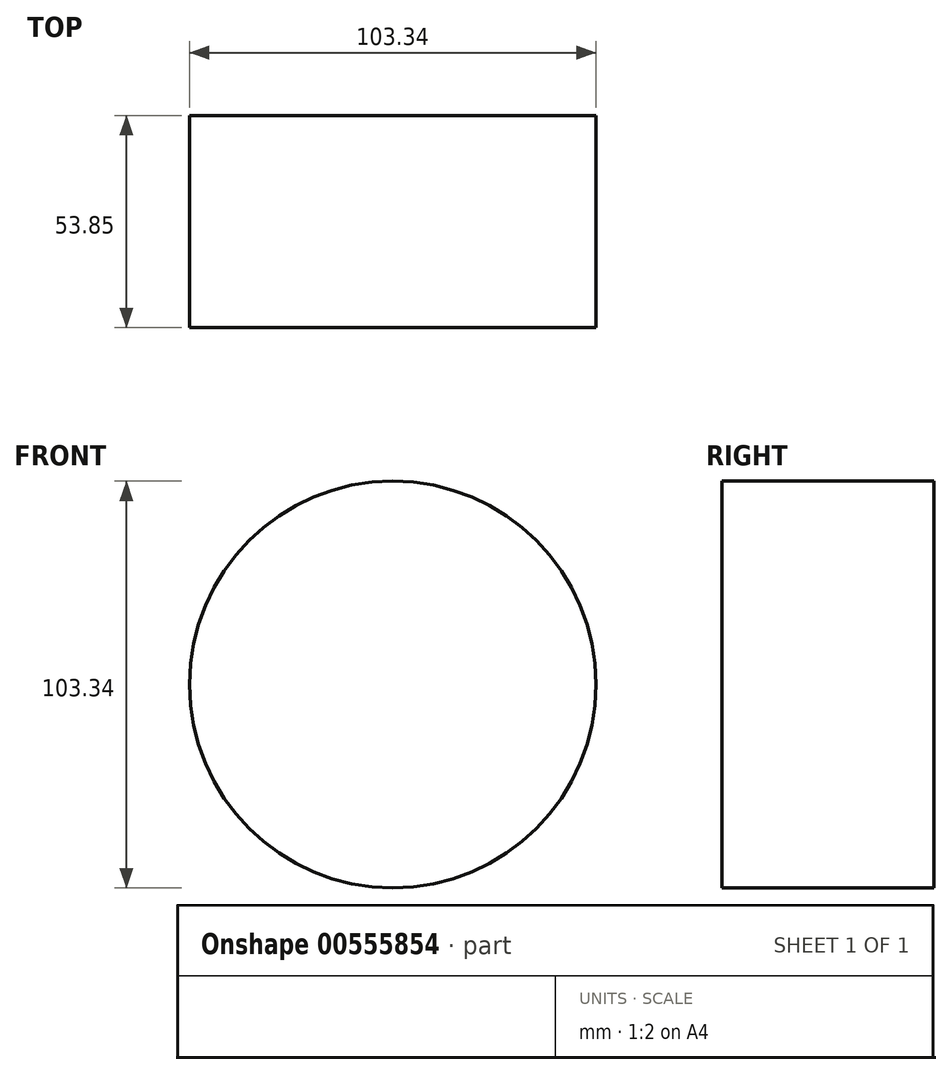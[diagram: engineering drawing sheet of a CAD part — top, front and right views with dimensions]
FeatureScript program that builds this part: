
annotation { "Feature Type Name" : "Feature", "Feature Type Description" : "" }
export const myFeature = defineFeature(function(context is Context, id is Id, definition is map)
    precondition{}
    {
        {
            var Q0;
            Q0=qCreatedBy(makeId("Front.planeOp"),FACE);
            var sketch = newSketch(context, id + "F0", { "sketchPlane" : qUnion([Q0])});
            skCircle(sketch, "E0", {"center": v(0, 0) * mm, "radius": 51.67 * mm});
            skSolve(sketch);
        }
        {
            var Q0;
            Q0 = qSketchRegion(id + "F0", true);
            extrude(context, id + "F1", {"entities" : qUnion([Q0]), "depth" : 53.85 * mm, "offsetDistance" : 25.4 * mm});
        }
    });
